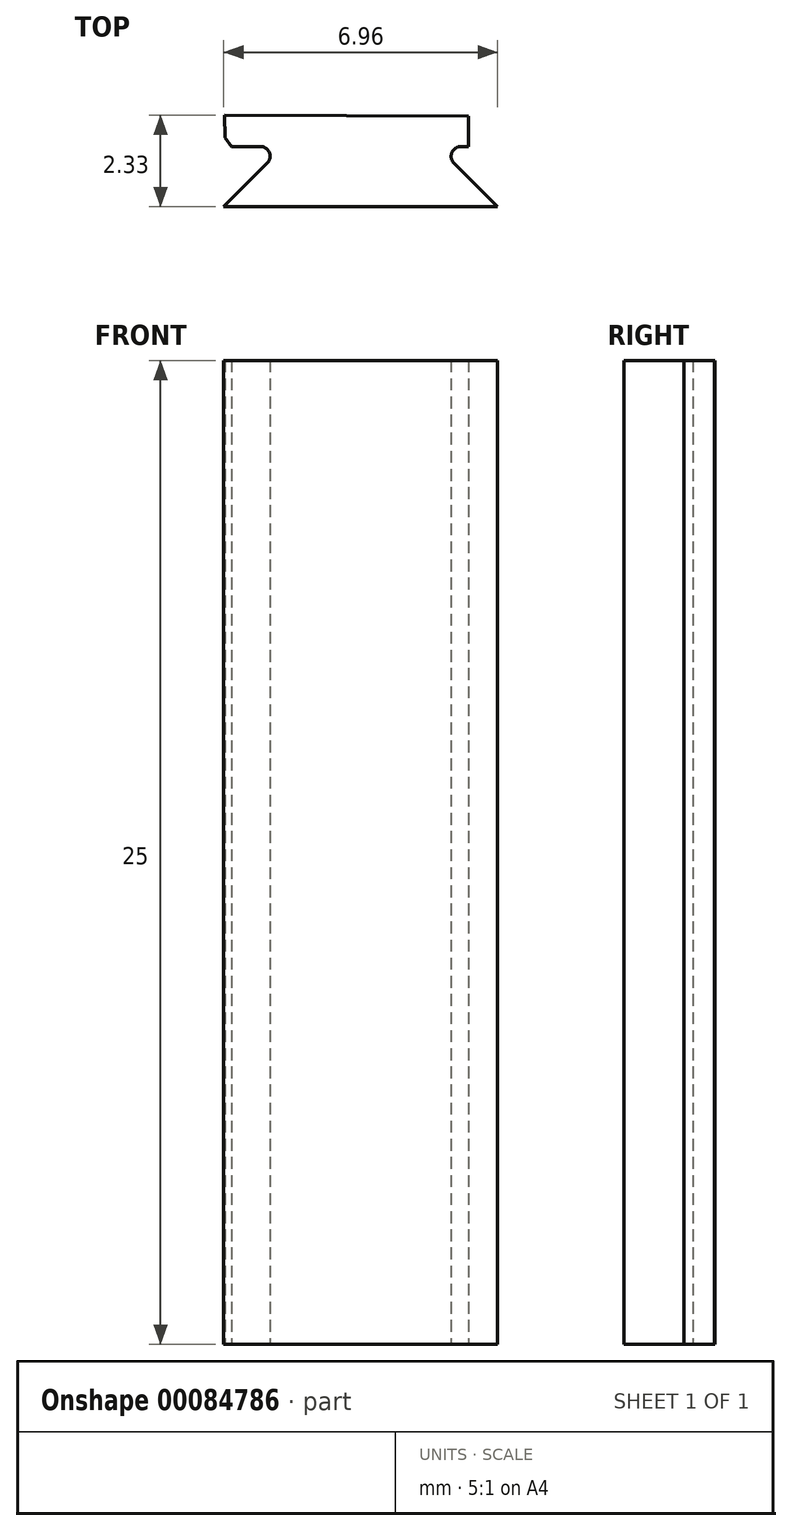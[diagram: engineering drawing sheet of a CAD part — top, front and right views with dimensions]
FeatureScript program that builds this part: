
annotation { "Feature Type Name" : "Feature", "Feature Type Description" : "" }
export const myFeature = defineFeature(function(context is Context, id is Id, definition is map)
    precondition{}
    {
        {
            var Q0;
            Q0=qCreatedBy(makeId("Top.planeOp"),FACE);
            var sketch = newSketch(context, id + "F0", { "sketchPlane" : qUnion([Q0])});
            skLineSegment(sketch, "E0", {"start": v(-68.58, -60.26) * mm, "end": v(-69.69, -61.37) * mm});
            skArc(sketch, "E1", {"start": v(-68.76, -59.84) * mm, "mid": v(-68.53, -59.99) * mm, "end": v(-68.58, -60.26) * mm});
            skLineSegment(sketch, "E2", {"start": v(-69.5, -59.84) * mm, "end": v(-68.76, -59.84) * mm});
            skArc(sketch, "E3", {"start": v(-63.66, -59.84) * mm, "mid": v(-63.9, -59.99) * mm, "end": v(-63.84, -60.26) * mm});
            skLineSegment(sketch, "E4", {"start": v(-63.84, -60.26) * mm, "end": v(-62.73, -61.37) * mm});
            skLineSegment(sketch, "E5", {"start": v(-69.69, -61.37) * mm, "end": v(-62.73, -61.37) * mm});
            skLineSegment(sketch, "E6", {"start": v(-69.5, -59.84) * mm, "end": v(-69.66, -59.6) * mm});
            skLineSegment(sketch, "E7", {"start": v(-63.47, -59.84) * mm, "end": v(-63.47, -59.06) * mm});
            skLineSegment(sketch, "E8", {"start": v(-63.47, -59.06) * mm, "end": v(-69.66, -59.04) * mm});
            skLineSegment(sketch, "E9", {"start": v(-69.66, -59.04) * mm, "end": v(-69.66, -59.6) * mm});
            skLineSegment(sketch, "E10", {"start": v(-63.47, -59.06) * mm, "end": v(-63.47, -59.84) * mm});
            skLineSegment(sketch, "E11.trimOffspring", {"start": v(-63.47, -59.84) * mm, "end": v(-63.66, -59.84) * mm});
            skSolve(sketch);
        }
        {
            var Q0;
            Q0=makeQuery(id+"F0.imprint","IMPRINT",FACE,{"disambiguationData":[TD([[makeQuery(id+"F0.imprint","IMPRINT",EDGE,{"derivedFrom":sQuery(id+"F0.wireOp",EDGE,"E0")}),1.0]])]});
            extrude(context, id + "F1", {"entities" : qUnion([Q0]), "depth" : 25 * mm});
        }
    });
